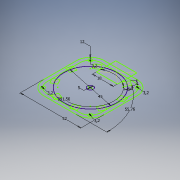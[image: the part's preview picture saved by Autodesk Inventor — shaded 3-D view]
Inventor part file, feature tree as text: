
AUTODESK INVENTOR PART (.ipt)
format: ipt  version: 2018 (Build 220112000, 112)  size: 125,440 bytes
history: native  units: mm
features: sketch x1
ambient origin geometry x8: Origin, YZ Plane, XZ Plane, XY Plane, X Axis, Y Axis, Z Axis, Center Point
feature tree (1):
  sketch  "Skizze1"  dims[d2=12.0mm d3=45.0mm d4=5.0mm d5=5.0mm d6=9.731956mm d7=18.0mm d8=80.0mm d10=50.876348mm d12=5.0mm d13=3.0mm d14=3.2mm d15=3.2mm d16=3.2mm d17=3.2mm d18=52.0mm]
